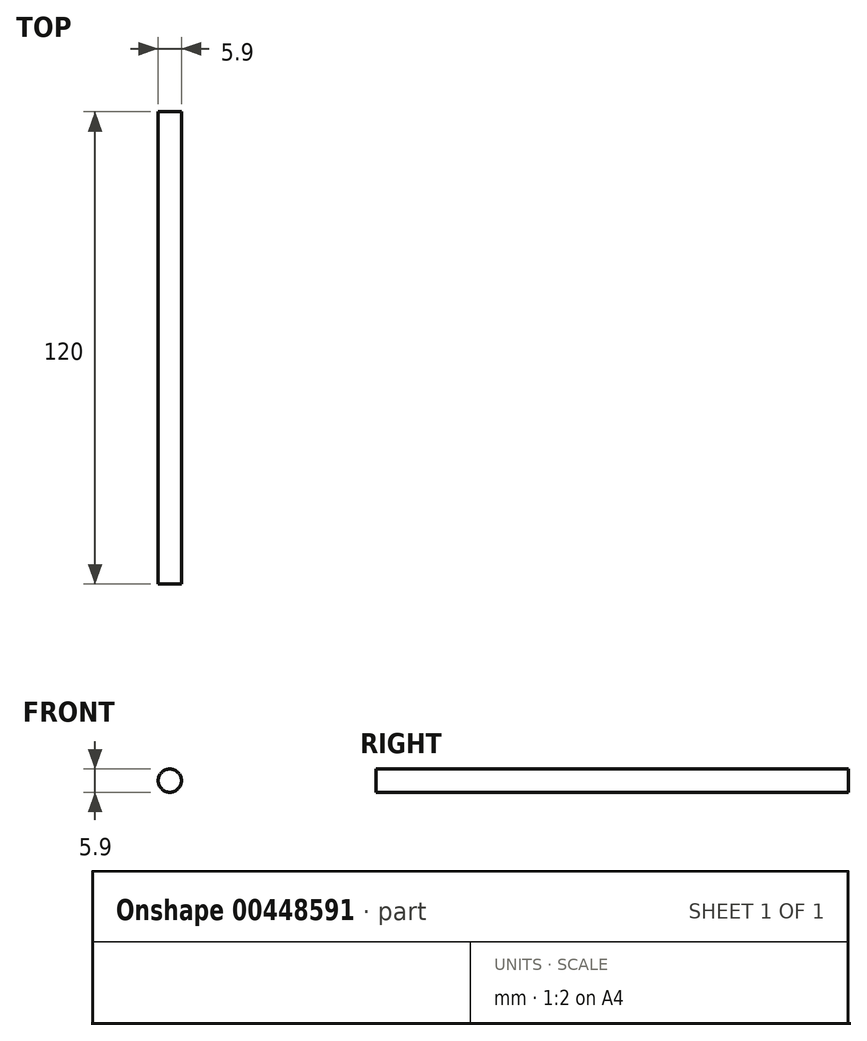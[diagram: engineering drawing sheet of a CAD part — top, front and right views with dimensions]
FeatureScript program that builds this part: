
annotation { "Feature Type Name" : "Feature", "Feature Type Description" : "" }
export const myFeature = defineFeature(function(context is Context, id is Id, definition is map)
    precondition{}
    {
        {
            var Q0;
            Q0=qCreatedBy(makeId("Front.planeOp"),FACE);
            var sketch = newSketch(context, id + "F0", { "sketchPlane" : qUnion([Q0])});
            skCircle(sketch, "E0", {"center": v(0, 0) * mm, "radius": 2.95 * mm});
            skSolve(sketch);
        }
        {
            var Q0;
            Q0=makeQuery(id+"F0.imprint","IMPRINT",FACE,{"disambiguationData":[TD([[makeQuery(id+"F0.imprint","IMPRINT",EDGE,{"derivedFrom":sQuery(id+"F0.wireOp",EDGE,"E0")}),1.0]])]});
            extrude(context, id + "F1", {"entities" : qUnion([Q0]), "depth" : 120 * mm});
        }
    });
